# Revit family: 2069462 Sylvania Lighting Fixture PIXER WALL 325x325 HO 1P 4000K DALI EMD
name_source: partatom
category: Lighting Fixtures
revit_build: Autodesk Revit 2016 (Build: 20150220_1215(x64)
units: mm (PartAtom-declared; Revit-internal decimal feet)

## family parameters
Cut with Voids When Loaded = No
Host = Face
Light Source = Yes
OmniClass Number = 23.80.70.00
OmniClass Title = Lighting
Part Type = Normal
Room Calculation Point = No
Round Connector Dimension = Use Diameter
Shared = No

## types (1)
- 2069462 PIXER W 325 HO 1P 4K DALI EMD
    Apparent Load = 16 VA
    Assembly Code = D5020200
    AssetType = Fixed
    ClassificationName = Uniclass2015
    ClassificationValue = EF_70_80
    Color Filter = 16777215
    Cost = 0 $
    Default Elevation = 1219 mm
    Dimming Lamp Color Temperature Shift = <None>
    DocumentationLiterature = http://www.sylvania-lighting.com
    DurationUnit = hours
    Emit Shape Visible in Rendering = No
    Emit from Circle Diameter = 610 mm
    ExpectedLife = 50000
    Height = 79 mm
    IfcExportAs = 120
    IfcExportType = IfcLightFixtureType
    ImpactProtectionIndex = Class II
    InputNominalFrequency = IK02
    InputVoltage = IP20
    Keynote = 0
    LampMacAdamStep = 16500
    LampNominalLuminous = LED
    Length = 257 mm  [stored 0.843176 ft]
    LightOutputRatio = 3
    LuminaireType = 1926 lm
    LuminousEfficacy = 100
    Material_1_FEILO = <By Category>
    Material_2_FEILO = <By Category>
    Material_3_FEILO = <By Category>
    Material_4_FEILO = <By Category>
    Model = PIXER WALL 325x325 HO 1P 4000K DALI EMD
    ModelNumber = 2069462
    ModelReference = PIXER WALL 325x325 HO 1P 4000K DALI EMD
    Name = PIXER WALL 325x325 HO 1P 4000K DALI EMD
    NominalDepth = 0 mm  [stored 0 ft]
    NominalHeight = 0 mm  [stored 0 ft]
    NominalLength = 0 mm  [stored 0 ft]
    Photometric Web File = 2069462.ies
    PowerConsumption = 257
    PowerFactor = 0
    Tilt Angle = 90.00°
    Type Image = <None>
    TypeName = PIXER WALL 325x325 HO 1P 4000K DALI EMD
    URL = 2069462.ies
    Voltage = 0 V
    WarrantyDescription = 0.92
    WarrantyDurationUnit = http://www.sylvania-lighting.com
    Width = 257 mm  [stored 0.843176 ft]

note: [stored X ft] marks values corroborated as IEEE doubles in the binary element streams (Revit-internal decimal feet)

## geometry (parser evidence)
native form markers: Sweep x2
no freeform markers — native parametric forms only
